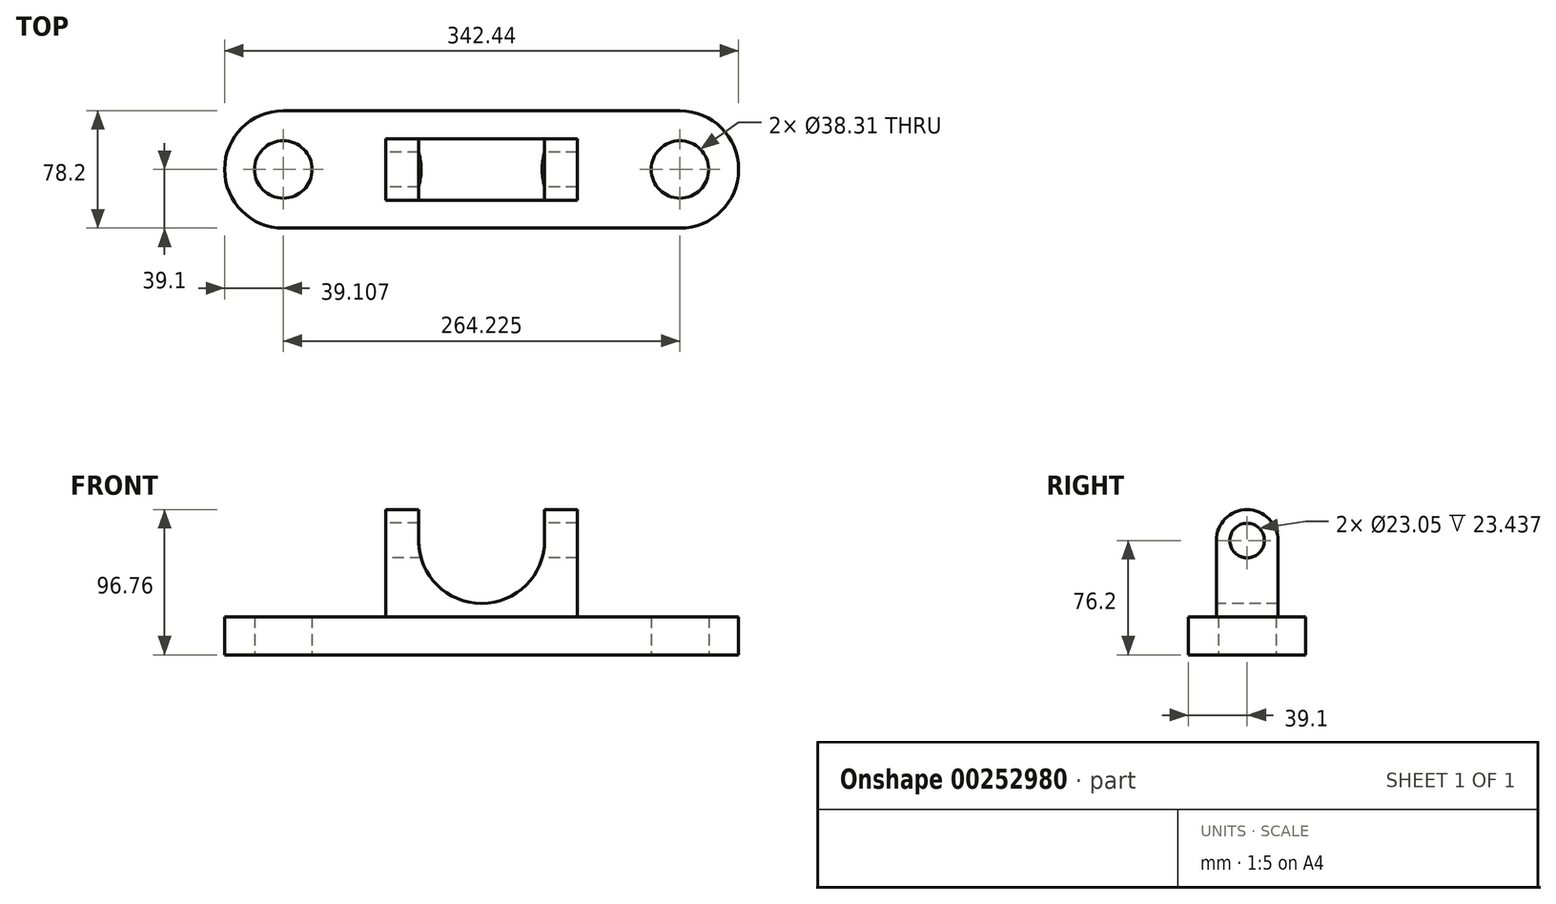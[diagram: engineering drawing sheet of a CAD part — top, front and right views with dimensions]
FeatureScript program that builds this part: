
annotation { "Feature Type Name" : "Feature", "Feature Type Description" : "" }
export const myFeature = defineFeature(function(context is Context, id is Id, definition is map)
    precondition{}
    {
        {
            var Q0;
            Q0=qCreatedBy(makeId("Top.planeOp"),FACE);
            var sketch = newSketch(context, id + "F0", { "sketchPlane" : qUnion([Q0])});
            skLineSegment(sketch, "E0.bottom", {"start": v(132.11, 39.1) * mm, "end": v(-132.11, 39.1) * mm});
            skLineSegment(sketch, "E0.top", {"start": v(132.11, -39.1) * mm, "end": v(-132.11, -39.1) * mm});
            skPoint(sketch, "E0.middle", {"position": v(0, 0) * mm});
            skArc(sketch, "E1", {"start": v(-132.11, 39.1) * mm, "mid": v(-171.22, 0) * mm, "end": v(-132.11, -39.1) * mm});
            skArc(sketch, "E2", {"start": v(132.11, -39.1) * mm, "mid": v(171.22, 0) * mm, "end": v(132.11, 39.1) * mm});
            skCircle(sketch, "E3", {"center": v(-132.11, 0) * mm, "radius": 19.16 * mm});
            skCircle(sketch, "E4.MirrorC", {"center": v(132.11, 0) * mm, "radius": 19.16 * mm});
            skSolve(sketch);
        }
        {
            var Q0;
            Q0=makeQuery(id+"F0.imprint","IMPRINT",FACE,{"disambiguationData":[TD([[makeQuery(id+"F0.imprint","IMPRINT",EDGE,{"derivedFrom":sQuery(id+"F0.wireOp",EDGE,"E0.bottom")}),1.0]])]});
            extrude(context, id + "F1", {"entities" : qUnion([Q0]), "depth" : 25.4 * mm});
        }
        {
            var Q0;
            Q0=makeQuery(id+"F1.opExtrude","CAP_FACE",FACE,{"disambiguationData":[OSD([sQuery(id+"F0.wireOp",EDGE,"E0.bottom"),sQuery(id+"F0.wireOp",EDGE,"E0.top"),sQuery(id+"F0.wireOp",EDGE,"E1"),sQuery(id+"F0.wireOp",EDGE,"E2"),sQuery(id+"F0.wireOp",EDGE,"E3"),sQuery(id+"F0.wireOp",EDGE,"E4.MirrorC")])],"isStart":false});
            var sketch = newSketch(context, id + "F2", { "sketchPlane" : qUnion([Q0])});
            skLineSegment(sketch, "E5.bottom", {"start": v(63.76, 20.56) * mm, "end": v(-63.76, 20.56) * mm});
            skLineSegment(sketch, "E5.top", {"start": v(63.76, -20.56) * mm, "end": v(-63.76, -20.56) * mm});
            skLineSegment(sketch, "E5.left", {"start": v(63.76, 20.56) * mm, "end": v(63.76, -20.56) * mm});
            skLineSegment(sketch, "E5.right", {"start": v(-63.76, 20.56) * mm, "end": v(-63.76, -20.56) * mm});
            skPoint(sketch, "E5.middle", {"position": v(0, 0) * mm});
            skSolve(sketch);
        }
        {
            var Q0;
            Q0=qSketchRegion(id+"F2",true);
            extrude(context, id + "F3", {"entities" : qUnion([Q0]), "operationType" : NewBodyOperationType.ADD, "depth" : 50.8 * mm});
        }
        {
            var Q0;
            Q0=makeQuery(id+"F3.opExtrude","SWEPT_FACE",FACE,{"disambiguationData":[OSD([sQuery(id+"F2.wireOp",EDGE,"E5.top")])]});
            var sketch = newSketch(context, id + "F4", { "sketchPlane" : qUnion([Q0])});
            skCircle(sketch, "E6", {"center": v(0, 76.2) * mm, "radius": 41.94 * mm});
            skSolve(sketch);
        }
        {
            var Q0;
            {var subQ0=sQuery(id+"F4.wireOp",EDGE,"E6");var subQ1=makeQuery(id+"F3.opExtrude","CAP_EDGE",EDGE,{"disambiguationData":[OSD([sQuery(id+"F2.wireOp",EDGE,"E5.top")])],"isStart":false});var subQ2=makeQuery(id+"F4.imprint","INTERSECT",VERTEX,{"disambiguationData":[OD(0.0)],"derivedFrom":[subQ1,subQ0]});Q0=makeQuery(id+"F4.imprint","IMPRINT",FACE,{"disambiguationData":[TD([[makeQuery(id+"F4.imprint","IMPRINT",EDGE,{"disambiguationData":[TD([[subQ2,1.0]])],"derivedFrom":subQ0}),1.0]])]});}
            extrude(context, id + "F5", {"entities" : qUnion([Q0]), "operationType" : NewBodyOperationType.REMOVE, "endBound" : BoundingType.THROUGH_ALL, "oppositeDirection" : true, "depth" : 25.4 * mm});
        }
        {
            var Q0;
            Q0=makeQuery(id+"F3.opExtrude","SWEPT_FACE",FACE,{"disambiguationData":[OSD([sQuery(id+"F2.wireOp",EDGE,"E5.right")])]});
            var sketch = newSketch(context, id + "F6", { "sketchPlane" : qUnion([Q0])});
            skArc(sketch, "E7", {"start": v(20.56, 76.2) * mm, "mid": v(0, 96.76) * mm, "end": v(-20.56, 76.2) * mm});
            skSolve(sketch);
        }
        {
            var Q0;
            Q0=makeQuery(id+"F6.imprint","IMPRINT",FACE,{"disambiguationData":[TD([[makeQuery(id+"F6.imprint","IMPRINT",EDGE,{"derivedFrom":sQuery(id+"F6.wireOp",EDGE,"E7")}),1.0]])]});
            var Q1;
            {var subQ0=sQuery(id+"F4.wireOp",EDGE,"E6");var subQ1=sQuery(id+"F2.wireOp",EDGE,"E5.top");Q1=makeQuery(id+"F5.boolean.opBoolean","COPY",VERTEX,{"derivedFrom":makeQuery(id+"F5.opExtrude","CAP_VERTEX",VERTEX,{"disambiguationData":[OSD([subQ1,subQ0]),TDD([makeQuery(id+"F4.imprint","INTERSECT",VERTEX,{"disambiguationData":[OD(1.0)],"derivedFrom":[makeQuery(id+"F3.opExtrude","CAP_EDGE",EDGE,{"disambiguationData":[OSD([subQ1])],"isStart":false}),subQ0]})])],"isStart":true})});}
            extrude(context, id + "F7", {"entities" : qUnion([Q0]), "operationType" : NewBodyOperationType.ADD, "endBound" : BoundingType.UP_TO_VERTEX, "oppositeDirection" : true, "endBoundEntityVertex" : qUnion([Q1]), "depth" : 25.4 * mm});
        }
        {
            var Q0;
            {var subQ0=sQuery(id+"F2.wireOp",EDGE,"E5.right");Q0=makeQuery(id+"F7.boolean.opBoolean","MERGE",FACE,{"derivedFrom":[makeQuery(id+"F3.opExtrude","SWEPT_FACE",FACE,{"disambiguationData":[OSD([subQ0])]}),makeQuery(id+"F7.opExtrude","CAP_FACE",FACE,{"disambiguationData":[OSD([subQ0,sQuery(id+"F6.wireOp",EDGE,"E7")])],"isStart":true})]});}
            var sketch = newSketch(context, id + "F8", { "sketchPlane" : qUnion([Q0])});
            skCircle(sketch, "E8", {"center": v(0, 76.2) * mm, "radius": 11.53 * mm});
            skSolve(sketch);
        }
        {
            var Q0;
            Q0=makeQuery(id+"F8.imprint","IMPRINT",FACE,{"disambiguationData":[TD([[makeQuery(id+"F8.imprint","IMPRINT",EDGE,{"derivedFrom":sQuery(id+"F8.wireOp",EDGE,"E8")}),1.0]])]});
            var Q1;
            Q1=sQuery(id+"F8.wireOp",EDGE,"E8");
            extrude(context, id + "F9", {"entities" : qUnion([Q0]), "operationType" : NewBodyOperationType.REMOVE, "surfaceEntities" : qUnion([Q1]), "endBound" : BoundingType.THROUGH_ALL, "oppositeDirection" : true, "depth" : 25.4 * mm});
        }
        {
            var Q0;
            Q0=makeQuery(id+"F3.opExtrude","SWEPT_FACE",FACE,{"disambiguationData":[OSD([sQuery(id+"F2.wireOp",EDGE,"E5.left")])]});
            var sketch = newSketch(context, id + "F10", { "sketchPlane" : qUnion([Q0])});
            skArc(sketch, "E9.0", {"start": v(-20.56, 76.2) * mm, "mid": v(0, 96.76) * mm, "end": v(20.56, 76.2) * mm});
            skArc(sketch, "E10.0", {"start": v(11.53, 76.2) * mm, "mid": v(0, 87.73) * mm, "end": v(-11.53, 76.2) * mm});
            skPoint(sketch, "E11.0", {"position": v(-16.04, 76.2) * mm});
            skLineSegment(sketch, "E12.0", {"start": v(-11.53, 76.2) * mm, "end": v(-20.56, 76.2) * mm});
            skLineSegment(sketch, "E13.0", {"start": v(20.56, 76.2) * mm, "end": v(11.53, 76.2) * mm});
            skSolve(sketch);
        }
        {
            var Q0;
            Q0=qSketchRegion(id+"F10",true);
            var Q1;
            Q1=makeQuery(id+"F5.boolean.opBoolean","INTERSECT",VERTEX,{"disambiguationData":[OD(0.0)],"derivedFrom":[makeQuery(id+"F3.opExtrude","SWEPT_FACE",FACE,{"disambiguationData":[OSD([sQuery(id+"F2.wireOp",EDGE,"E5.bottom")])]}),makeQuery(id+"F5.opExtrude","SWEPT_FACE",FACE,{"disambiguationData":[OSD([sQuery(id+"F4.wireOp",EDGE,"E6")])]})]});
            extrude(context, id + "F11", {"entities" : qUnion([Q0]), "operationType" : NewBodyOperationType.ADD, "endBound" : BoundingType.UP_TO_VERTEX, "oppositeDirection" : true, "endBoundEntityVertex" : qUnion([Q1]), "depth" : 25.4 * mm});
        }
    });
